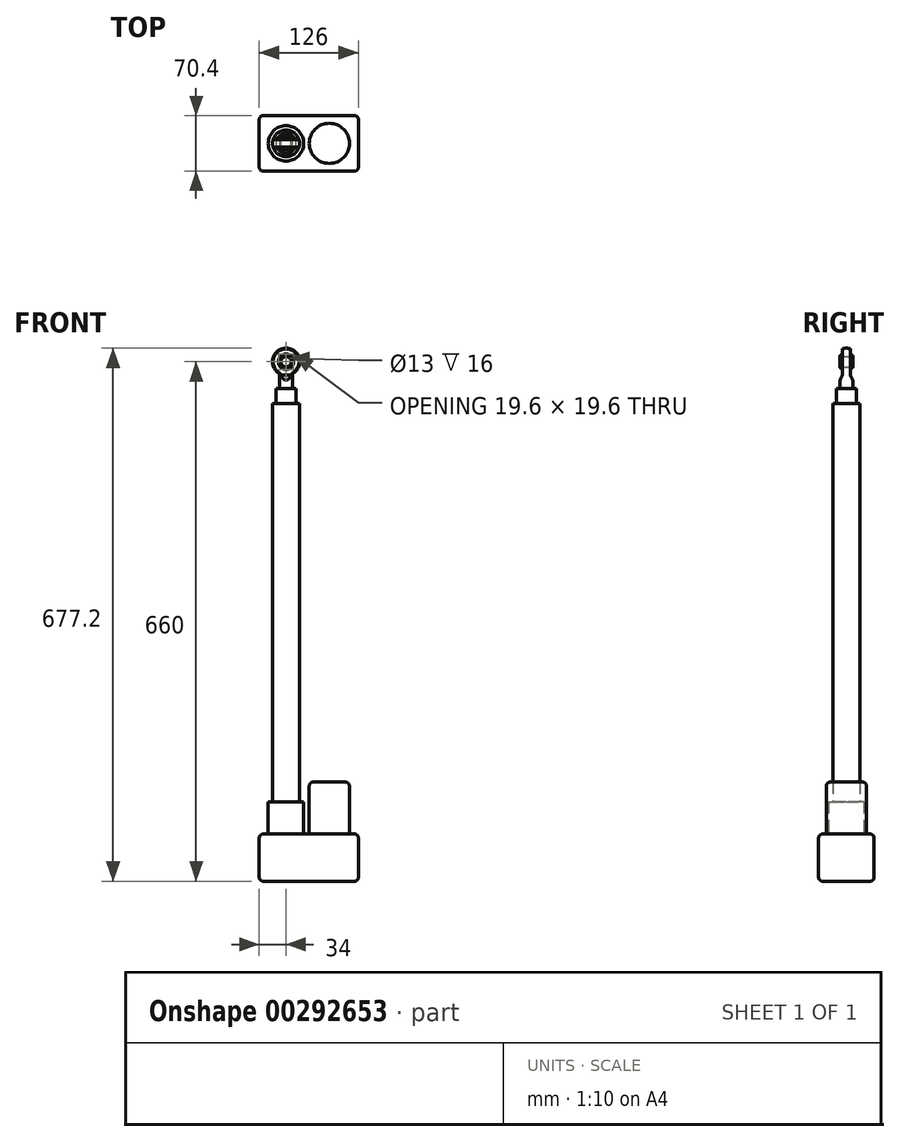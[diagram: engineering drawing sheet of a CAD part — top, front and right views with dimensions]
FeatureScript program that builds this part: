
annotation { "Feature Type Name" : "Feature", "Feature Type Description" : "" }
export const myFeature = defineFeature(function(context is Context, id is Id, definition is map)
    precondition{}
    {
        {
            var Q0;
            Q0=qCreatedBy(makeId("Top.planeOp"),FACE);
            var sketch = newSketch(context, id + "F0", { "sketchPlane" : qUnion([Q0])});
            skCircle(sketch, "E0", {"center": v(0, 0) * mm, "radius": 12.7 * mm});
            skSolve(sketch);
        }
        {
            var Q0;
            Q0=makeQuery(id+"F0.imprint","IMPRINT",FACE,{"disambiguationData":[TD([[makeQuery(id+"F0.imprint","IMPRINT",EDGE,{"derivedFrom":sQuery(id+"F0.wireOp",EDGE,"E0")}),1.0]])]});
            extrude(context, id + "F1", {"entities" : qUnion([Q0]), "depth" : 620 * mm});
        }
        {
            var Q0;
            Q0=qCreatedBy(makeId("Top.planeOp"),FACE);
            var sketch = newSketch(context, id + "F2", { "sketchPlane" : qUnion([Q0])});
            skCircle(sketch, "E1", {"center": v(0, 0) * mm, "radius": 17 * mm});
            skSolve(sketch);
        }
        {
            var Q0;
            Q0 = qSketchRegion(id + "F2", true);
            extrude(context, id + "F3", {"entities" : qUnion([Q0]), "depth" : 607 * mm});
        }
        {
            var Q0;
            Q0=qCreatedBy(makeId("Front.planeOp"),FACE);
            var sketch = newSketch(context, id + "F4", { "sketchPlane" : qUnion([Q0])});
            skLineSegment(sketch, "E2", {"start": v(0, 620) * mm, "end": v(0, 659) * mm});
            skLineSegment(sketch, "E3", {"start": v(0, 620) * mm, "end": v(8.1, 620) * mm});
            skLineSegment(sketch, "E4", {"start": v(8.1, 626) * mm, "end": v(8.1, 644.83) * mm});
            skArc(sketch, "E5", {"start": v(8.1, 644.83) * mm, "mid": v(16.69, 664.17) * mm, "end": v(0, 677.2) * mm});
            skArc(sketch, "E6", {"start": v(0, 659) * mm, "mid": v(1, 660) * mm, "end": v(0, 661) * mm});
            skLineSegment(sketch, "E7", {"start": v(0, 677.2) * mm, "end": v(0, 661) * mm});
            skLineSegment(sketch, "E8", {"start": v(0, 842.33) * mm, "end": v(0, 620) * mm, "construction": true});
            skLineSegment(sketch, "E9", {"start": v(8.1, 626) * mm, "end": v(12.7, 626) * mm});
            skLineSegment(sketch, "E10", {"start": v(12.7, 626) * mm, "end": v(12.7, 620) * mm});
            skLineSegment(sketch, "E11", {"start": v(12.7, 620) * mm, "end": v(8.1, 620) * mm});
            skSolve(sketch);
        }
        {
            var Q0;
            Q0 = qSketchRegion(id + "F4", true);
            var Q1;
            Q1=sQuery(id+"F4.wireOp",EDGE,"E8");
            revolve(context, id + "F5", {"operationType" : NewBodyOperationType.ADD, "entities" : qUnion([Q0]), "axis" : qUnion([Q1]), "revolveType" : RevolveType.FULL});
        }
        {
            var Q0;
            Q0=qCreatedBy(makeId("Right.planeOp"),FACE);
            var sketch = newSketch(context, id + "F6", { "sketchPlane" : qUnion([Q0])});
            skLineSegment(sketch, "E12", {"start": v(5, 967.2) * mm, "end": v(5, 643) * mm});
            skLineSegment(sketch, "E13", {"start": v(5, 643) * mm, "end": v(8.34, 636) * mm});
            skLineSegment(sketch, "E14", {"start": v(8.34, 636) * mm, "end": v(23, 636) * mm});
            skLineSegment(sketch, "E15", {"start": v(23, 636) * mm, "end": v(23, 967) * mm});
            skLineSegment(sketch, "E16", {"start": v(23, 967) * mm, "end": v(5, 967.2) * mm});
            skLineSegment(sketch, "E17", {"start": v(0, 901.88) * mm, "end": v(0, 996.28) * mm, "construction": true});
            skLineSegment(sketch, "E18.MirrorCS", {"start": v(-23, 967) * mm, "end": v(-5, 967.2) * mm});
            skLineSegment(sketch, "E19.MirrorCS", {"start": v(-8.34, 636) * mm, "end": v(-23, 636) * mm});
            skLineSegment(sketch, "E20.MirrorCS", {"start": v(-5, 967.2) * mm, "end": v(-5, 643) * mm});
            skLineSegment(sketch, "E21.MirrorCS", {"start": v(-5, 643) * mm, "end": v(-8.34, 636) * mm});
            skLineSegment(sketch, "E22.MirrorCS", {"start": v(-23, 636) * mm, "end": v(-23, 967) * mm});
            skSolve(sketch);
        }
        {
            var Q0;
            Q0 = qSketchRegion(id + "F6", true);
            extrude(context, id + "F7", {"entities" : qUnion([Q0]), "operationType" : NewBodyOperationType.REMOVE, "endBound" : BoundingType.THROUGH_ALL, "oppositeDirection" : true, "depth" : 25 * mm, "hasSecondDirection" : true, "secondDirectionBound" : SecondDirectionBoundingType.THROUGH_ALL, "secondDirectionOppositeDirection" : false, "secondDirectionDepth" : 25 * mm});
        }
        {
            var Q0;
            Q0=qCreatedBy(makeId("Front.planeOp"),FACE);
            var sketch = newSketch(context, id + "F8", { "sketchPlane" : qUnion([Q0])});
            skCircle(sketch, "E23", {"center": v(0, 660) * mm, "radius": 6.5 * mm});
            skSolve(sketch);
        }
        {
            var Q0;
            Q0 = qSketchRegion(id + "F8", true);
            extrude(context, id + "F9", {"entities" : qUnion([Q0]), "operationType" : NewBodyOperationType.REMOVE, "endBound" : BoundingType.THROUGH_ALL, "depth" : 25 * mm, "hasSecondDirection" : true, "secondDirectionBound" : SecondDirectionBoundingType.THROUGH_ALL, "secondDirectionOppositeDirection" : true, "secondDirectionDepth" : 25 * mm});
        }
        {
            var Q0;
            Q0=makeQuery(id+"F7.boolean.opBoolean","SPLIT",EDGE,{"disambiguationData":[OD(1.0)],"derivedFrom":makeQuery(id+"F5.opRevolve","SWEPT_EDGE",EDGE,{"disambiguationData":[OSD([sQuery(id+"F4.wireOp",EDGE,"E4"),sQuery(id+"F4.wireOp",EDGE,"E5")])]})});
            var Q1;
            Q1=makeQuery(id+"F7.boolean.opBoolean","SPLIT",EDGE,{"disambiguationData":[OD(0.0)],"derivedFrom":makeQuery(id+"F5.opRevolve","SWEPT_EDGE",EDGE,{"disambiguationData":[OSD([sQuery(id+"F4.wireOp",EDGE,"E4"),sQuery(id+"F4.wireOp",EDGE,"E5")])]})});
            fillet(context, id + "F10", {"entities" : qUnion([Q0, Q1]), "radius" : 5 * mm, "tangentPropagation" : true, "allowEdgeOverflow" : false});
        }
        {
            var Q0;
            Q0=qCreatedBy(makeId("Top.planeOp"),FACE);
            var sketch = newSketch(context, id + "F11", { "sketchPlane" : qUnion([Q0])});
            skLineSegment(sketch, "E24.bottom", {"start": v(-34, -35.2) * mm, "end": v(92, -35.2) * mm});
            skLineSegment(sketch, "E24.top", {"start": v(-34, 35.2) * mm, "end": v(92, 35.2) * mm});
            skLineSegment(sketch, "E24.left", {"start": v(-34, -35.2) * mm, "end": v(-34, 35.2) * mm});
            skLineSegment(sketch, "E24.right", {"start": v(92, -35.2) * mm, "end": v(92, 35.2) * mm});
            skPoint(sketch, "E24.middle", {"position": v(29, 0) * mm});
            skSolve(sketch);
        }
        {
            var Q0;
            Q0 = qSketchRegion(id + "F11", true);
            extrude(context, id + "F12", {"entities" : qUnion([Q0]), "operationType" : NewBodyOperationType.ADD, "depth" : 60 * mm});
        }
        {
            var Q0;
            Q0=makeQuery(id+"F12.opExtrude","CAP_FACE",FACE,{"disambiguationData":[OSD([sQuery(id+"F11.wireOp",EDGE,"E24.bottom"),sQuery(id+"F11.wireOp",EDGE,"E24.top"),sQuery(id+"F11.wireOp",EDGE,"E24.left"),sQuery(id+"F11.wireOp",EDGE,"E24.right")])],"isStart":false});
            var sketch = newSketch(context, id + "F13", { "sketchPlane" : qUnion([Q0])});
            skCircle(sketch, "E25", {"center": v(55, 0) * mm, "radius": 25.5 * mm});
            skSolve(sketch);
        }
        {
            var Q0;
            Q0 = qSketchRegion(id + "F13", true);
            extrude(context, id + "F14", {"entities" : qUnion([Q0]), "operationType" : NewBodyOperationType.ADD, "depth" : 66 * mm});
        }
        {
            var Q0;
            Q0=makeQuery(id+"F12.opExtrude","CAP_FACE",FACE,{"disambiguationData":[OSD([sQuery(id+"F11.wireOp",EDGE,"E24.bottom"),sQuery(id+"F11.wireOp",EDGE,"E24.top"),sQuery(id+"F11.wireOp",EDGE,"E24.left"),sQuery(id+"F11.wireOp",EDGE,"E24.right")])],"isStart":false});
            var sketch = newSketch(context, id + "F15", { "sketchPlane" : qUnion([Q0])});
            skCircle(sketch, "E26", {"center": v(0, 0) * mm, "radius": 22.5 * mm});
            skSolve(sketch);
        }
        {
            var Q0;
            Q0=makeQuery(id+"F15.imprint","IMPRINT",FACE,{"disambiguationData":[TD([[makeQuery(id+"F15.imprint","IMPRINT",EDGE,{"derivedFrom":makeQuery(id+"F12.boolean.opBoolean","INTERSECT",EDGE,{"derivedFrom":[makeQuery(id+"F3.opExtrude","SWEPT_FACE",FACE,{"disambiguationData":[OSD([sQuery(id+"F2.wireOp",EDGE,"E1")])]}),makeQuery(id+"F12.opExtrude","CAP_FACE",FACE,{"disambiguationData":[OSD([sQuery(id+"F11.wireOp",EDGE,"E24.bottom"),sQuery(id+"F11.wireOp",EDGE,"E24.top"),sQuery(id+"F11.wireOp",EDGE,"E24.left"),sQuery(id+"F11.wireOp",EDGE,"E24.right")])],"isStart":false})]})}),1.0]])]});
            var Q1;
            Q1=makeQuery(id+"F15.imprint","IMPRINT",FACE,{"disambiguationData":[TD([[makeQuery(id+"F15.imprint","IMPRINT",EDGE,{"derivedFrom":sQuery(id+"F15.wireOp",EDGE,"E26")}),1.0]])]});
            extrude(context, id + "F16", {"entities" : qUnion([Q0, Q1]), "operationType" : NewBodyOperationType.ADD, "depth" : 41 * mm});
        }
        {
            var Q0;
            Q0=makeQuery(id+"F12.opExtrude","SWEPT_EDGE",EDGE,{"disambiguationData":[OSD([sQuery(id+"F11.wireOp",EDGE,"E24.bottom"),sQuery(id+"F11.wireOp",EDGE,"E24.right")])]});
            var Q1;
            Q1=makeQuery(id+"F12.opExtrude","SWEPT_EDGE",EDGE,{"disambiguationData":[OSD([sQuery(id+"F11.wireOp",EDGE,"E24.top"),sQuery(id+"F11.wireOp",EDGE,"E24.right")])]});
            var Q2;
            Q2=makeQuery(id+"F14.opExtrude","CAP_EDGE",EDGE,{"disambiguationData":[OSD([sQuery(id+"F13.wireOp",EDGE,"E25")])],"isStart":false});
            var Q3;
            Q3=makeQuery(id+"F12.opExtrude","SWEPT_EDGE",EDGE,{"disambiguationData":[OSD([sQuery(id+"F11.wireOp",EDGE,"E24.bottom"),sQuery(id+"F11.wireOp",EDGE,"E24.left")])]});
            var Q4;
            Q4=makeQuery(id+"F12.opExtrude","SWEPT_EDGE",EDGE,{"disambiguationData":[OSD([sQuery(id+"F11.wireOp",EDGE,"E24.top"),sQuery(id+"F11.wireOp",EDGE,"E24.left")])]});
            var Q5;
            Q5=makeQuery(id+"F12.boolean.opBoolean","MERGE",FACE,{"derivedFrom":[makeQuery(id+"F3.opExtrude","CAP_FACE",FACE,{"disambiguationData":[OSD([sQuery(id+"F2.wireOp",EDGE,"E1")])],"isStart":true}),makeQuery(id+"F12.opExtrude","CAP_FACE",FACE,{"disambiguationData":[OSD([sQuery(id+"F11.wireOp",EDGE,"E24.bottom"),sQuery(id+"F11.wireOp",EDGE,"E24.top"),sQuery(id+"F11.wireOp",EDGE,"E24.left"),sQuery(id+"F11.wireOp",EDGE,"E24.right")])],"isStart":true})]});
            fillet(context, id + "F17", {"entities" : qUnion([Q0, Q1, Q2, Q3, Q4, Q5]), "radius" : 5 * mm, "tangentPropagation" : true, "allowEdgeOverflow" : false});
        }
        {
            var Q0;
            Q0=makeQuery(id+"F12.opExtrude","CAP_EDGE",EDGE,{"disambiguationData":[OSD([sQuery(id+"F11.wireOp",EDGE,"E24.top")])],"isStart":false});
            fillet(context, id + "F18", {"entities" : qUnion([Q0]), "radius" : 5 * mm, "tangentPropagation" : true, "allowEdgeOverflow" : false});
        }
        {
            var Q0;
            Q0 = qSketchRegion(id + "F6", true);
            extrude(context, id + "F19", {"entities" : qUnion([Q0]), "operationType" : NewBodyOperationType.REMOVE, "oppositeDirection" : true, "depth" : 25 * mm, "hasSecondDirection" : true, "secondDirectionOppositeDirection" : false, "secondDirectionDepth" : 25 * mm});
        }
        {
            var Q0;
            Q0=qCreatedBy(makeId("Right.planeOp"),FACE);
            var sketch = newSketch(context, id + "F20", { "sketchPlane" : qUnion([Q0])});
            skLineSegment(sketch, "E27", {"start": v(3, 660) * mm, "end": v(-14.4, 660) * mm, "construction": true});
            skLineSegment(sketch, "E28", {"start": v(-8, 666.5) * mm, "end": v(8, 666.5) * mm});
            skLineSegment(sketch, "E29", {"start": v(8, 666.5) * mm, "end": v(8, 667.55) * mm});
            skLineSegment(sketch, "E30", {"start": v(-8, 666.5) * mm, "end": v(-8, 667.55) * mm});
            skArc(sketch, "E31", {"start": v(8, 667.55) * mm, "mid": v(0, 671) * mm, "end": v(-8, 667.55) * mm});
            skSolve(sketch);
        }
        {
            var Q0;
            Q0 = qSketchRegion(id + "F20", true);
            var Q1;
            Q1=sQuery(id+"F20.wireOp",EDGE,"E27");
            revolve(context, id + "F21", {"operationType" : NewBodyOperationType.ADD, "entities" : qUnion([Q0]), "axis" : qUnion([Q1]), "revolveType" : RevolveType.FULL});
        }
    });
